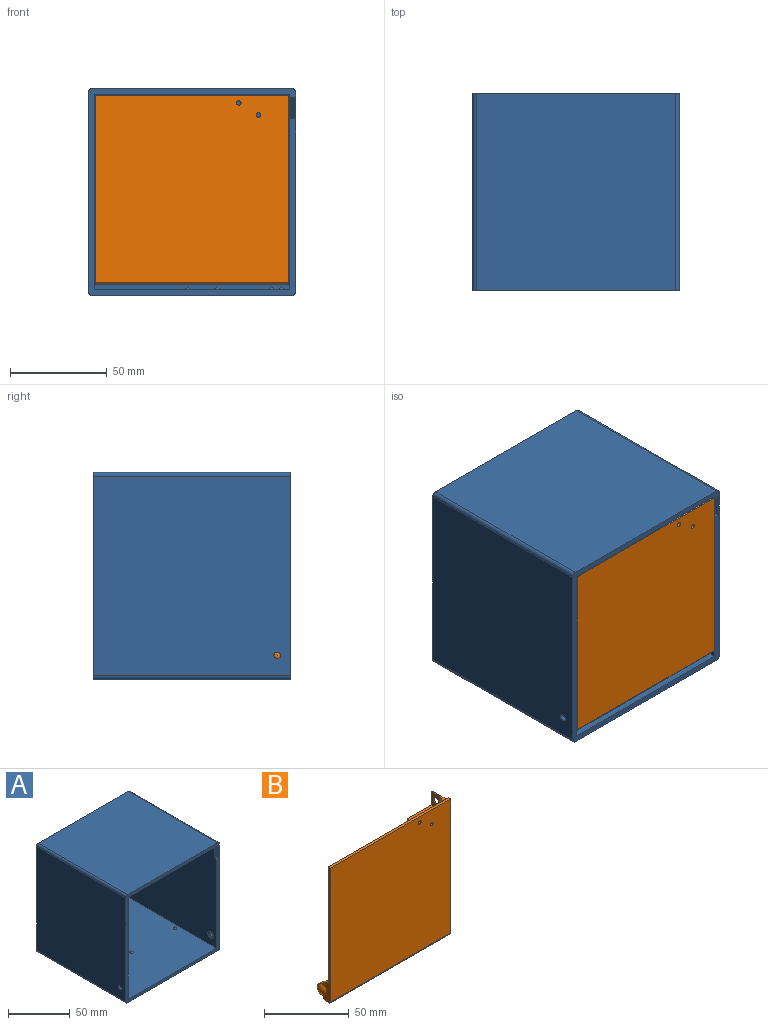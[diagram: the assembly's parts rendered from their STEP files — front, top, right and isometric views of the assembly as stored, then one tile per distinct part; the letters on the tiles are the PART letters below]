
ASSEMBLY  parts=2 mates=1
PART A: 28 faces, bbox 107x102x107 mm
  f0: plane 107x107mm, normal (0,-1,0), area 1211mm2, adj f1,f2,f3,f4,f5,f6,f7,f8
  f1: cylinder r=2mm len=102mm, axis (0,-1,0), area 320.4mm2, adj f0,f2,f12,f14
  f2: plane 103x102mm, normal (0,0,-1), area 10506mm2, adj f0,f1,f3,f14
  f3: cylinder r=2mm len=102mm, axis (0,-1,0), area 320.4mm2, adj f0,f2,f4,f14
  f4: plane 103x102mm, normal (1,0,0), area 10496.9mm2, adj f0,f3,f5,f14,f23,f26
  f5: cylinder r=2mm len=102mm, axis (0,-1,0), area 320.4mm2, adj f0,f4,f6,f14
  f6: plane 103x102mm, normal (0,0,1), area 10506mm2, adj f0,f5,f7,f14
  f7: cylinder r=2mm len=102mm, axis (0,-1,0), area 320.4mm2, adj f0,f6,f12,f14
  f8: plane 101x100mm, normal (0,0,1), area 10071.7mm2, adj f0,f9,f11,f13,f15,f16,f17,f18
  f9: plane 101x100mm, normal (1,0,0), area 10063.1mm2, adj f0,f8,f10,f13,f19
  f10: plane 101x100mm, normal (0,0,-1), area 10100mm2, adj f0,f9,f11,f13
  f11: plane 101x100mm, normal (-1,0,0), area 10011.4mm2, adj f0,f8,f10,f13,f20,f21,f22,f23
  f12: plane 103x102mm, normal (-1,0,0), area 10496.9mm2, adj f0,f1,f7,f14,f27
  f13: plane 101x101mm, normal (0,-1,0), area 10201mm2, adj f8,f9,f10,f11
  f14: plane 107x107mm, normal (0,1,0), area 11445.6mm2, adj f1,f2,f3,f4,f5,f6,f7,f12
  f15: cone r=1.5mm half-angle=40deg, axis (0,0,-1), area 11mm2, adj f8
  f16: cone r=1.5mm half-angle=40deg, axis (0,0,-1), area 11mm2, adj f8
  f17: cone r=1.5mm half-angle=40deg, axis (0,0,-1), area 11mm2, adj f8
  f18: cone r=1.5mm half-angle=40deg, axis (0,0,-1), area 11mm2, adj f8
  f19: sphere r=5.66mm, area 31.8mm2, adj f9,f27
  f20: sphere r=5.66mm, area 31.8mm2, adj f11,f26
  f21: plane 3x3mm, normal (0,0,-1), area 4.5mm2, adj f0,f11,f23
  f22: plane 3x3mm, normal (0,0,1), area 4.5mm2, adj f0,f11,f23
  f23: plane 11.2x3mm, normal (-0.71,-0.71,0), area 47.5mm2, adj f4,f11,f21,f22
  f24: cylinder r=2.4mm len=4.8mm, axis (-1,0,0), area 30.2mm2, adj f11,f25
  f25: plane 4.8x4.8mm, normal (-1,0,0), area 18.1mm2, adj f24
  f26: cylinder r=1.7mm len=3.4mm, axis (-1,0,0), area 22.5mm2, adj f4,f20
  f27: cylinder r=1.7mm len=3.4mm, axis (-1,0,0), area 22.5mm2, adj f12,f19
PART B: 30 faces, bbox 103.3x15x97.6 mm
  f0: plane 100x97.6mm, normal (0,1,0), area 9412.1mm2, adj f1,f2,f4,f5,f6,f7,f8,f10
  f1: plane 97.6x9mm, normal (-1,0,0), area 230.6mm2, adj f0,f3,f4,f10,f11,f13,f15,f26
  f2: plane 97.6x15.05mm, normal (1,0,0), area 340.4mm2, adj f0,f3,f4,f10,f16,f17,f20,f21
  f3: plane 100x96.6mm, normal (0,-1,0), area 9651.7mm2, adj f1,f2,f4,f26,f27,f28
  f4: plane 100x2mm, normal (0,0,1), area 200mm2, adj f0,f1,f2,f3
  f5: plane 20x3mm, normal (0,0,1), area 60mm2, adj f0,f6,f8,f9
  f6: plane 11.2x3mm, normal (-1,0,0), area 33.6mm2, adj f0,f5,f7,f9
  f7: plane 20x3mm, normal (0,0,-1), area 60mm2, adj f0,f6,f8,f9
  f8: plane 11.2x3mm, normal (1,0,0), area 33.6mm2, adj f0,f5,f7,f9
  f9: plane 20x11.2mm, normal (0,1,0), area 215.7mm2, adj f5,f6,f7,f8,f27,f28
  f10: plane 100x2.56mm, normal (0,0,-1), area 109.4mm2, adj f0,f1,f2,f13,f14,f17,f19,f26
  f11: plane 7x4.04mm, normal (0,0.5,0.87), area 24.2mm2, adj f0,f1,f12,f14
  f12: cylinder r=4mm len=6.93mm, axis (-1,0,0), area 25.1mm2, adj f11,f13,f14,f15
  f13: plane 5.44x3.14mm, normal (0,0.5,-0.87), area 18.8mm2, adj f1,f10,f12,f14
  f14: plane 14.11x9mm, normal (1,0,0), area 85.9mm2, adj f0,f10,f11,f12,f13
  f15: sphere r=5.66mm, area 58.9mm2, adj f1,f12
  f16: plane 7x4.04mm, normal (0,0.5,0.87), area 24.2mm2, adj f0,f2,f18,f19
  f17: plane 5.44x3.14mm, normal (0,0.5,-0.87), area 18.8mm2, adj f2,f10,f18,f19
  f18: cylinder r=4mm len=6.93mm, axis (1,0,0), area 25.1mm2, adj f16,f17,f19,f20
  f19: plane 14.11x9mm, normal (-1,0,0), area 85.9mm2, adj f0,f10,f16,f17,f18
  f20: sphere r=5.66mm, area 58.9mm2, adj f2,f18
  f21: plane 13.05x4mm, normal (0,0,1), area 22mm2, adj f0,f2,f24,f25,f29
  f22: plane 13.05x4mm, normal (0,0,-1), area 22mm2, adj f0,f2,f24,f25,f29
  f23: cylinder r=2.4mm len=4.8mm, axis (1,0,0), area 15.1mm2, adj f2,f25
  f24: plane 9.8x1mm, normal (0,1,0), area 9.8mm2, adj f2,f21,f22,f25
  f25: plane 9.8x7.05mm, normal (-1,0,0), area 51mm2, adj f21,f22,f23,f24,f29
  f26: cylinder r=1mm len=100mm, axis (1,0,0), area 157.1mm2, adj f1,f2,f3,f10
  f27: cylinder r=1.15mm len=5mm, axis (0,1,0), area 36.1mm2, adj f3,f9
  f28: cylinder r=1.15mm len=5mm, axis (0,1,0), area 36.1mm2, adj f3,f9
  f29: plane 9.8x6mm, normal (-0.89,0.45,0), area 65.7mm2, adj f0,f21,f22,f25
PLACE A at identity
PLACE B at identity
MATE revolute B.f12 <-> A.f26  axis (-1,0,0) through (-50,5,9.01)mm
